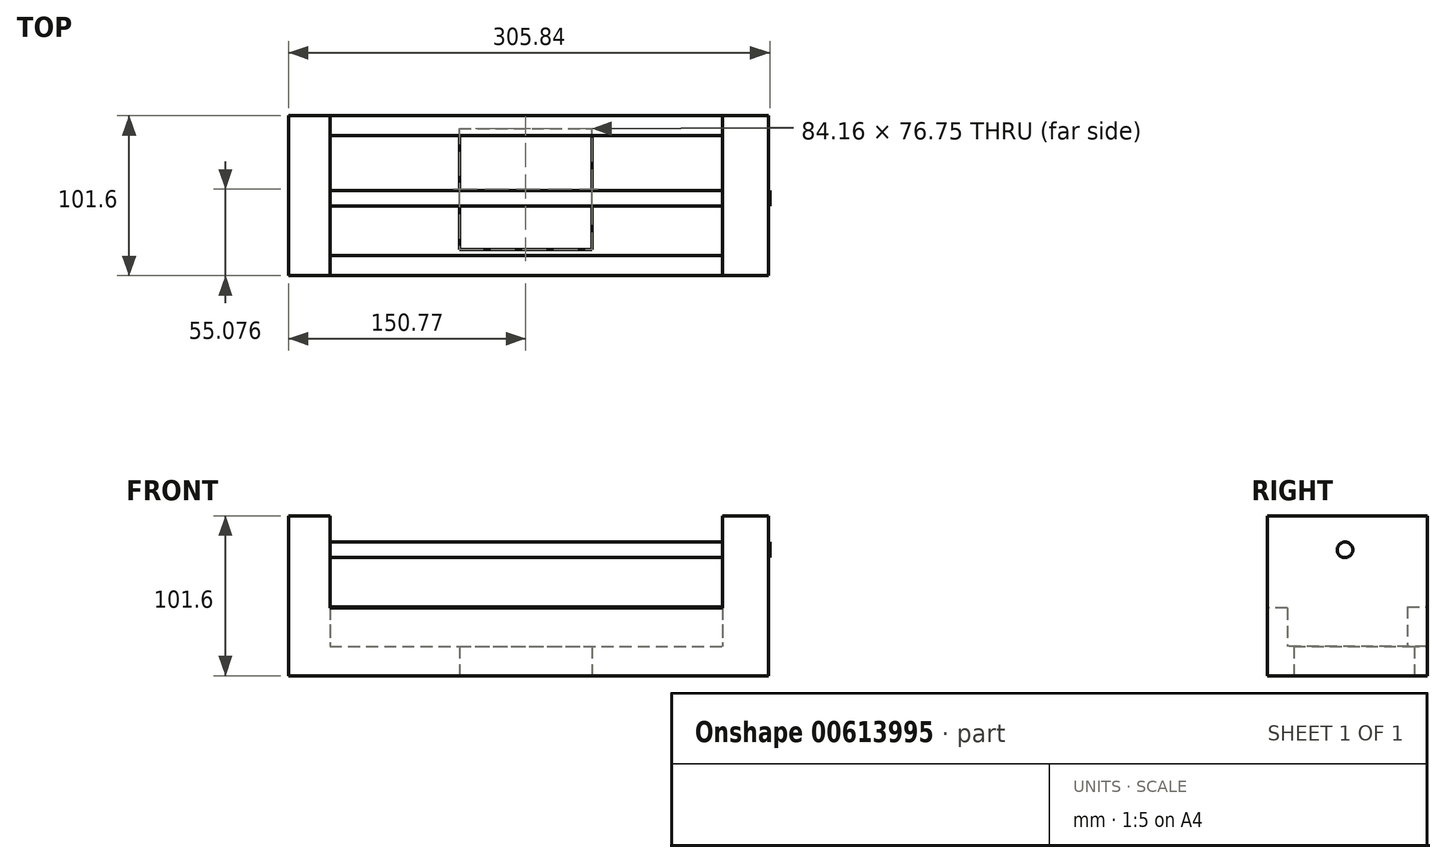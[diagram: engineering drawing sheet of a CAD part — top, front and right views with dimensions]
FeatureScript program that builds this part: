
annotation { "Feature Type Name" : "Feature", "Feature Type Description" : "" }
export const myFeature = defineFeature(function(context is Context, id is Id, definition is map)
    precondition{}
    {
        {
            var Q0;
            Q0=qCreatedBy(makeId("Front.planeOp"),FACE);
            var sketch = newSketch(context, id + "F0", { "sketchPlane" : qUnion([Q0])});
            skLineSegment(sketch, "E0.bottom", {"start": v(-148.6, 11.89) * mm, "end": v(156.2, 11.89) * mm});
            skLineSegment(sketch, "E0.top", {"start": v(-148.6, -89.71) * mm, "end": v(156.2, -89.71) * mm});
            skLineSegment(sketch, "E0.left", {"start": v(-148.6, 11.89) * mm, "end": v(-148.6, -89.71) * mm});
            skLineSegment(sketch, "E0.right", {"start": v(156.2, 11.89) * mm, "end": v(156.2, -89.71) * mm});
            skSolve(sketch);
        }
        {
            var Q0;
            Q0=makeQuery(id+"F0.imprint","IMPRINT",FACE,{"disambiguationData":[TD([[makeQuery(id+"F0.imprint","IMPRINT",EDGE,{"derivedFrom":sQuery(id+"F0.wireOp",EDGE,"E0.bottom")}),-1.0]])]});
            extrude(context, id + "F1", {"entities" : qUnion([Q0]), "oppositeDirection" : true, "depth" : 101.6 * mm, "offsetDistance" : 25.4 * mm});
        }
        {
            var Q0;
            Q0=makeQuery(id+"F1.opExtrude","CAP_FACE",FACE,{"disambiguationData":[OSD([sQuery(id+"F0.wireOp",EDGE,"E0.bottom"),sQuery(id+"F0.wireOp",EDGE,"E0.top"),sQuery(id+"F0.wireOp",EDGE,"E0.left"),sQuery(id+"F0.wireOp",EDGE,"E0.right")])],"isStart":true});
            var sketch = newSketch(context, id + "F2", { "sketchPlane" : qUnion([Q0])});
            skLineSegment(sketch, "E1.bottom", {"start": v(-122.15, 11.89) * mm, "end": v(127.28, 11.89) * mm});
            skLineSegment(sketch, "E1.top", {"start": v(-122.15, -71.05) * mm, "end": v(127.28, -71.05) * mm});
            skLineSegment(sketch, "E1.left", {"start": v(-122.15, 11.89) * mm, "end": v(-122.15, -71.05) * mm});
            skLineSegment(sketch, "E1.right", {"start": v(127.28, 11.89) * mm, "end": v(127.28, -71.05) * mm});
            skSolve(sketch);
        }
        {
            var Q0;
            Q0=makeQuery(id+"F2.imprint","IMPRINT",FACE,{"disambiguationData":[TD([[makeQuery(id+"F2.imprint","IMPRINT",EDGE,{"derivedFrom":sQuery(id+"F2.wireOp",EDGE,"E1.bottom")}),-1.0]])]});
            extrude(context, id + "F3", {"entities" : qUnion([Q0]), "operationType" : NewBodyOperationType.REMOVE, "oppositeDirection" : true, "depth" : 101.6 * mm, "offsetDistance" : 25.4 * mm});
        }
        {
            var Q0;
            Q0=makeQuery(id+"F1.opExtrude","SWEPT_FACE",FACE,{"disambiguationData":[OSD([sQuery(id+"F0.wireOp",EDGE,"E0.top")])]});
            var sketch = newSketch(context, id + "F4", { "sketchPlane" : qUnion([Q0])});
            skLineSegment(sketch, "E2.bottom", {"start": v(-39.9, -16.7) * mm, "end": v(44.26, -16.7) * mm});
            skLineSegment(sketch, "E2.top", {"start": v(-39.9, -93.45) * mm, "end": v(44.26, -93.45) * mm});
            skLineSegment(sketch, "E2.left", {"start": v(-39.9, -16.7) * mm, "end": v(-39.9, -93.45) * mm});
            skLineSegment(sketch, "E2.right", {"start": v(44.26, -16.7) * mm, "end": v(44.26, -93.45) * mm});
            skSolve(sketch);
        }
        {
            var Q0;
            Q0=makeQuery(id+"F4.imprint","IMPRINT",FACE,{"disambiguationData":[TD([[makeQuery(id+"F4.imprint","IMPRINT",EDGE,{"derivedFrom":sQuery(id+"F4.wireOp",EDGE,"E2.bottom")}),-1.0]])]});
            extrude(context, id + "F5", {"entities" : qUnion([Q0]), "operationType" : NewBodyOperationType.REMOVE, "oppositeDirection" : true, "depth" : 25.4 * mm, "offsetDistance" : 25.4 * mm});
        }
        {
            var Q0;
            Q0=makeQuery(id+"F1.opExtrude","CAP_FACE",FACE,{"disambiguationData":[OSD([sQuery(id+"F0.wireOp",EDGE,"E0.bottom"),sQuery(id+"F0.wireOp",EDGE,"E0.top"),sQuery(id+"F0.wireOp",EDGE,"E0.left"),sQuery(id+"F0.wireOp",EDGE,"E0.right")])],"isStart":true});
            var sketch = newSketch(context, id + "F6", { "sketchPlane" : qUnion([Q0])});
            skLineSegment(sketch, "E3.bottom", {"start": v(-122.15, -46.71) * mm, "end": v(127.28, -46.71) * mm});
            skLineSegment(sketch, "E3.top", {"start": v(-122.15, -71.05) * mm, "end": v(127.28, -71.05) * mm});
            skLineSegment(sketch, "E3.left", {"start": v(-122.15, -46.71) * mm, "end": v(-122.15, -71.05) * mm});
            skLineSegment(sketch, "E3.right", {"start": v(127.28, -46.71) * mm, "end": v(127.28, -71.05) * mm});
            skSolve(sketch);
        }
        {
            var Q0;
            Q0=makeQuery(id+"F6.imprint","IMPRINT",FACE,{"disambiguationData":[TD([[makeQuery(id+"F6.imprint","IMPRINT",EDGE,{"derivedFrom":sQuery(id+"F6.wireOp",EDGE,"E3.bottom")}),-1.0]])]});
            extrude(context, id + "F7", {"entities" : qUnion([Q0]), "operationType" : NewBodyOperationType.ADD, "oppositeDirection" : true, "depth" : 12.7 * mm, "offsetDistance" : 25.4 * mm});
        }
        {
            var Q0;
            Q0=makeQuery(id+"F1.opExtrude","CAP_FACE",FACE,{"disambiguationData":[OSD([sQuery(id+"F0.wireOp",EDGE,"E0.bottom"),sQuery(id+"F0.wireOp",EDGE,"E0.top"),sQuery(id+"F0.wireOp",EDGE,"E0.left"),sQuery(id+"F0.wireOp",EDGE,"E0.right")])],"isStart":false});
            var sketch = newSketch(context, id + "F8", { "sketchPlane" : qUnion([Q0])});
            skLineSegment(sketch, "E4.bottom", {"start": v(-127.28, -45.88) * mm, "end": v(122.15, -45.88) * mm});
            skLineSegment(sketch, "E4.top", {"start": v(-127.28, -71.05) * mm, "end": v(122.15, -71.05) * mm});
            skLineSegment(sketch, "E4.left", {"start": v(-127.28, -45.88) * mm, "end": v(-127.28, -71.05) * mm});
            skLineSegment(sketch, "E4.right", {"start": v(122.15, -45.88) * mm, "end": v(122.15, -71.05) * mm});
            skSolve(sketch);
        }
        {
            var Q0;
            Q0=makeQuery(id+"F8.imprint","IMPRINT",FACE,{"disambiguationData":[TD([[makeQuery(id+"F8.imprint","IMPRINT",EDGE,{"derivedFrom":sQuery(id+"F8.wireOp",EDGE,"E4.bottom")}),-1.0]])]});
            extrude(context, id + "F9", {"entities" : qUnion([Q0]), "oppositeDirection" : true, "depth" : 12.7 * mm, "offsetDistance" : 25.4 * mm});
        }
        {
            var Q0;
            Q0=makeQuery(id+"F3.boolean.opBoolean","COPY",FACE,{"derivedFrom":makeQuery(id+"F3.opExtrude","SWEPT_FACE",FACE,{"disambiguationData":[OSD([sQuery(id+"F2.wireOp",EDGE,"E1.left")])]})});
            var sketch = newSketch(context, id + "F10", { "sketchPlane" : qUnion([Q0])});
            skCircle(sketch, "E5", {"center": v(49.27, -9.7) * mm, "radius": 4.95 * mm});
            skSolve(sketch);
        }
        {
            var Q0;
            Q0=makeQuery(id+"F10.imprint","IMPRINT",FACE,{"disambiguationData":[TD([[makeQuery(id+"F10.imprint","IMPRINT",EDGE,{"derivedFrom":sQuery(id+"F10.wireOp",EDGE,"E5")}),1.0]])]});
            extrude(context, id + "F11", {"entities" : qUnion([Q0]), "operationType" : NewBodyOperationType.ADD, "depth" : 279.4 * mm, "offsetDistance" : 25.4 * mm});
        }
    });
